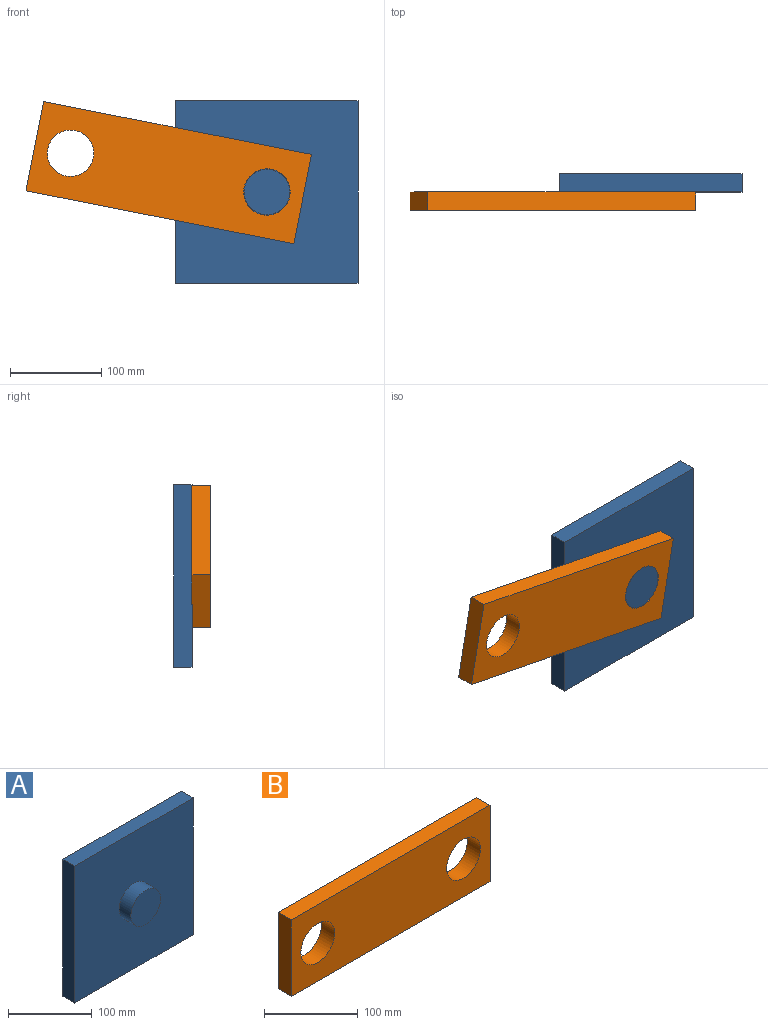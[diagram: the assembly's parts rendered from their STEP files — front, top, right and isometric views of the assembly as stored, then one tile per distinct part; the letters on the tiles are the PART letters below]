
ASSEMBLY  parts=2 mates=1
PART A: 8 faces, bbox 200x40x200 mm
  f0: plane 200x20mm, normal (-1,0,0), area 4000mm2, adj f1,f3,f4,f5
  f1: plane 200x20mm, normal (0,0,-1), area 4000mm2, adj f0,f2,f4,f5
  f2: plane 200x20mm, normal (1,0,0), area 4000mm2, adj f1,f3,f4,f5
  f3: plane 200x20mm, normal (0,0,1), area 4000mm2, adj f0,f2,f4,f5
  f4: plane 200x200mm, normal (0,-1,0), area 38036.5mm2, adj f0,f1,f2,f3,f6
  f5: plane 200x200mm, normal (0,1,0), area 40000mm2, adj f0,f1,f2,f3
  f6: cylinder r=25mm len=50mm, axis (0,1,0), area 3141.6mm2, adj f4,f7
  f7: plane 50x50mm, normal (0,-1,0), area 1963.5mm2, adj f6
PART B: 8 faces, bbox 300x20x100 mm
  f0: plane 100x20mm, normal (-1,0,0), area 2000mm2, adj f1,f5,f6,f7
  f1: plane 300x20mm, normal (0,0,-1), area 6000mm2, adj f0,f2,f6,f7
  f2: plane 100x20mm, normal (1,0,0), area 2000mm2, adj f1,f5,f6,f7
  f3: cylinder r=25.5mm len=51mm, axis (0,1,0), area 3204.4mm2, adj f6,f7
  f4: cylinder r=25.5mm len=51mm, axis (0,1,0), area 3204.4mm2, adj f6,f7
  f5: plane 300x20mm, normal (0,0,1), area 6000mm2, adj f0,f2,f6,f7
  f6: plane 300x100mm, normal (0,-1,0), area 25914.4mm2, adj f0,f1,f2,f3,f4,f5
  f7: plane 300x100mm, normal (0,1,0), area 25914.4mm2, adj f0,f1,f2,f3,f4,f5
PLACE A t=(-41.18,89.33,-46.94)mm fixed
PLACE B rot(axis=(0,1,0),11.2deg) t=(-205.94,69.33,54.3)mm
MATE revolute B.f4 <-> A.f6  axis (0,-1,0) through (58.82,49.33,53.06)mm
